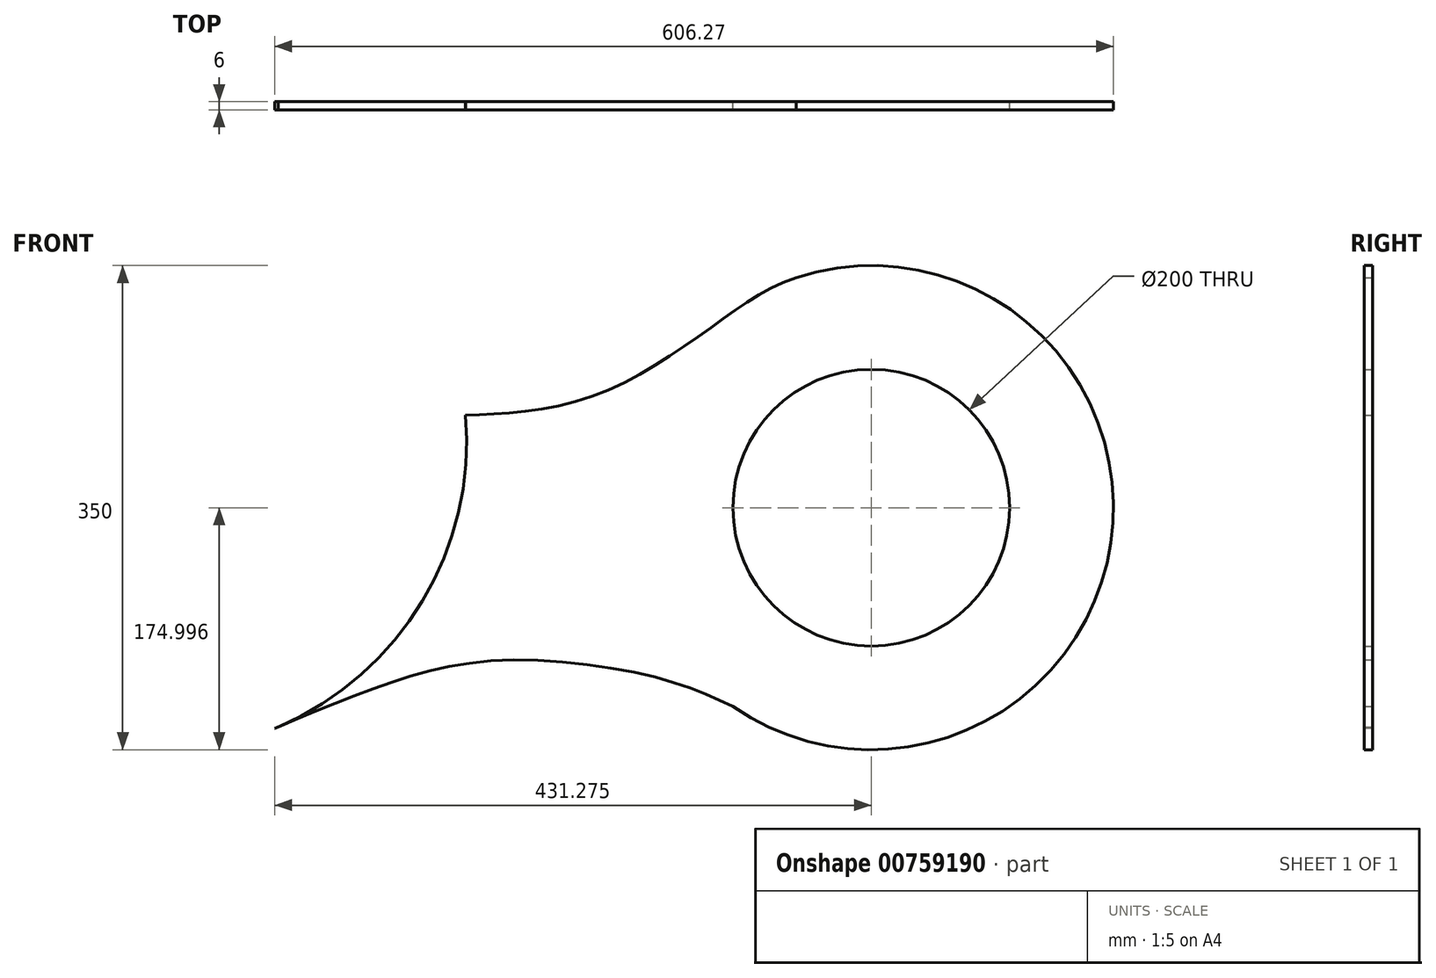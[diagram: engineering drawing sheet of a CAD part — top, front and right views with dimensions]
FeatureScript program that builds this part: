
annotation { "Feature Type Name" : "Feature", "Feature Type Description" : "" }
export const myFeature = defineFeature(function(context is Context, id is Id, definition is map)
    precondition{}
    {
        {
            var Q0;
            Q0=qCreatedBy(makeId("Front.planeOp"),FACE);
            var sketch = newSketch(context, id + "F0", { "sketchPlane" : qUnion([Q0])});
            skArc(sketch, "E0", {"start": v(79.07, -139.6) * mm, "mid": v(352.17, -21.48) * mm, "end": v(124.77, 170.4) * mm});
            skCircle(sketch, "E1", {"center": v(179.04, 4.04) * mm, "radius": 100 * mm});
            skFitSpline(sketch, "E2", {"points": [v(-114.15, 71) * mm, v(-25.76, 83.45) * mm, v(64.2, 135.03) * mm, v(124.77, 170.4) * mm], "startDerivative": vector(217.3, 5.56) * mm, "endDerivative": vector(222.4, 75.34) * mm});
            skFitSpline(sketch, "E3", {"points": [v(-252.23, -155.58) * mm, v(-172.15, -123.73) * mm, v(-87.6, -106.29) * mm, v(26.57, -119.5) * mm, v(79.07, -139.6) * mm], "startDerivative": vector(319.22, 134.84) * mm, "endDerivative": vector(224.63, -103.35) * mm});
            skArc(sketch, "E4", {"start": v(-252.23, -155.58) * mm, "mid": v(-146.24, -64.8) * mm, "end": v(-114.15, 71) * mm});
            skSolve(sketch);
        }
        {
            var Q0;
            Q0 = qSketchRegion(id + "F0", true);
            extrude(context, id + "F1", {"entities" : qUnion([Q0]), "depth" : 6 * mm, "offsetDistance" : 25 * mm});
        }
    });
